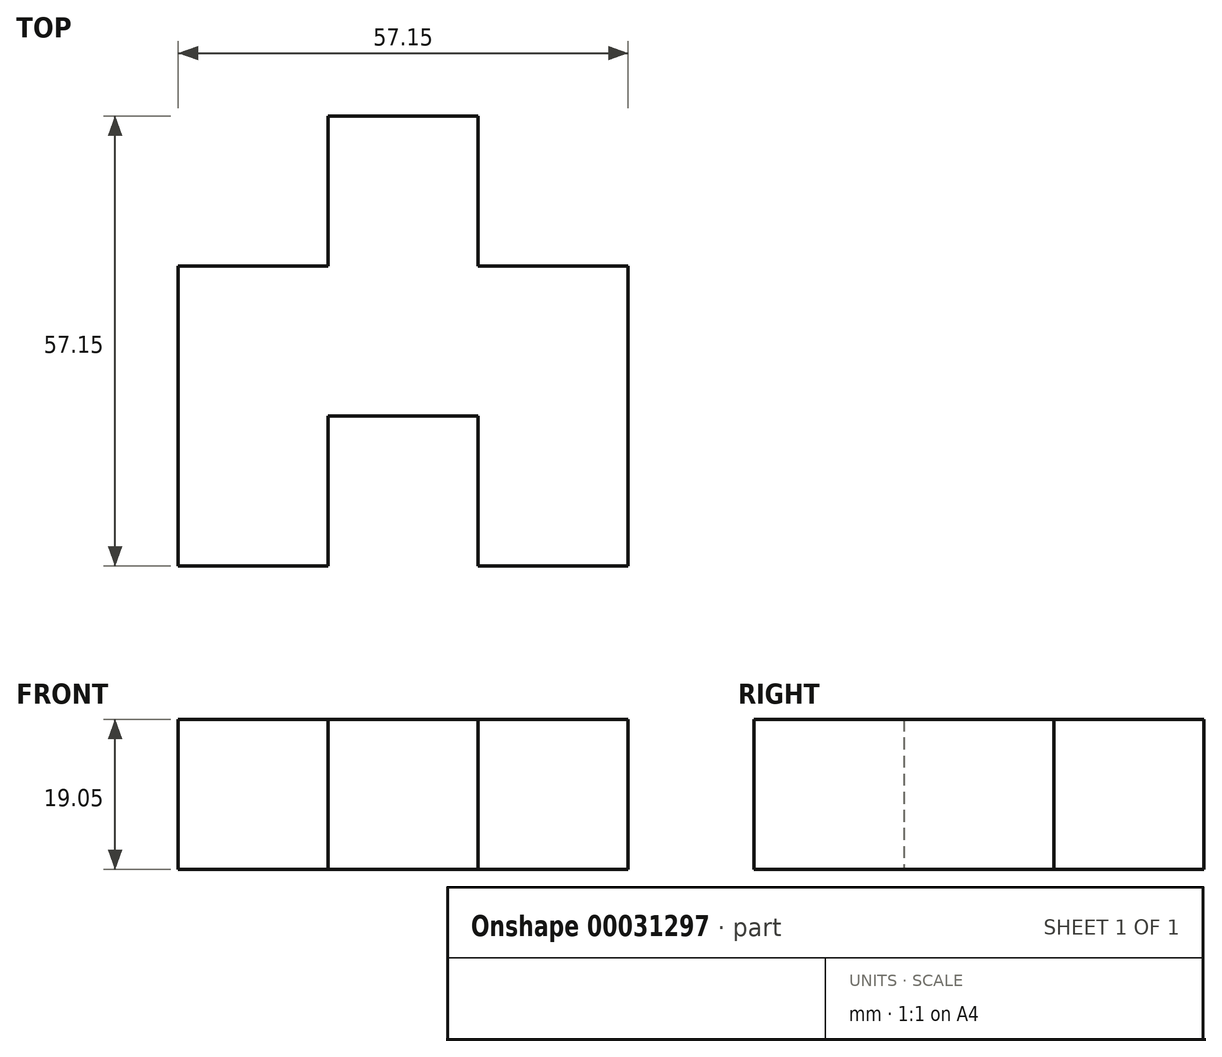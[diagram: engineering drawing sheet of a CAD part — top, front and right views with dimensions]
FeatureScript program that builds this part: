
annotation { "Feature Type Name" : "Feature", "Feature Type Description" : "" }
export const myFeature = defineFeature(function(context is Context, id is Id, definition is map)
    precondition{}
    {
        {
            var Q0;
            Q0=qCreatedBy(makeId("Top.planeOp"),FACE);
            var sketch = newSketch(context, id + "F0", { "sketchPlane" : qUnion([Q0])});
            skLineSegment(sketch, "E0", {"start": v(0, 0) * mm, "end": v(0, 38.1) * mm});
            skLineSegment(sketch, "E1", {"start": v(0, 38.1) * mm, "end": v(19.05, 38.1) * mm});
            skLineSegment(sketch, "E2", {"start": v(19.05, 38.1) * mm, "end": v(19.05, 57.15) * mm});
            skLineSegment(sketch, "E3", {"start": v(19.05, 57.15) * mm, "end": v(38.1, 57.15) * mm});
            skLineSegment(sketch, "E4", {"start": v(38.1, 57.15) * mm, "end": v(38.1, 38.1) * mm});
            skLineSegment(sketch, "E5", {"start": v(38.1, 38.1) * mm, "end": v(57.15, 38.1) * mm});
            skLineSegment(sketch, "E6", {"start": v(57.15, 38.1) * mm, "end": v(57.15, 0) * mm});
            skLineSegment(sketch, "E7", {"start": v(57.15, 0) * mm, "end": v(38.1, 0) * mm});
            skLineSegment(sketch, "E8", {"start": v(38.1, 0) * mm, "end": v(38.1, 19.05) * mm});
            skLineSegment(sketch, "E9", {"start": v(38.1, 19.05) * mm, "end": v(19.05, 19.05) * mm});
            skLineSegment(sketch, "E10", {"start": v(19.05, 19.05) * mm, "end": v(19.05, 0) * mm});
            skLineSegment(sketch, "E11", {"start": v(19.05, 0) * mm, "end": v(0, 0) * mm});
            skSolve(sketch);
        }
        {
            var Q0;
            Q0=makeQuery(id+"F0.imprint","IMPRINT",FACE,{"disambiguationData":[TD([[makeQuery(id+"F0.imprint","IMPRINT",EDGE,{"derivedFrom":sQuery(id+"F0.wireOp",EDGE,"E0")}),-1.0]])]});
            extrude(context, id + "F1", {"entities" : qUnion([Q0]), "depth" : 19.05 * mm});
        }
    });
